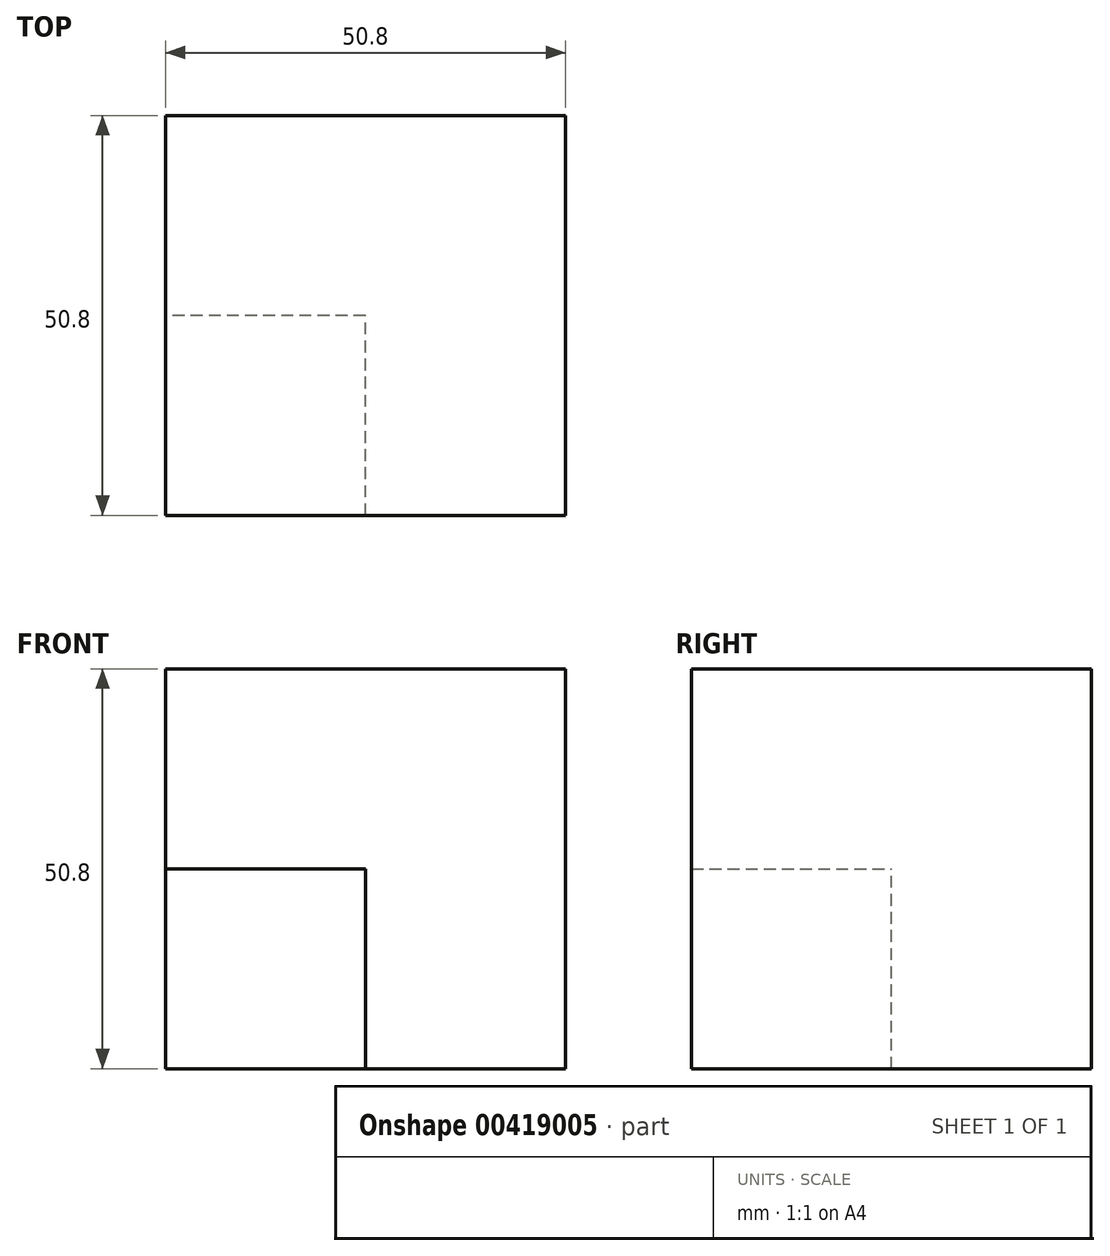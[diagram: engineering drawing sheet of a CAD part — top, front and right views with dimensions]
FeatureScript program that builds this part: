
annotation { "Feature Type Name" : "Feature", "Feature Type Description" : "" }
export const myFeature = defineFeature(function(context is Context, id is Id, definition is map)
    precondition{}
    {
        {
            var Q0;
            Q0=qCreatedBy(makeId("Right.planeOp"),FACE);
            var sketch = newSketch(context, id + "F0", { "sketchPlane" : qUnion([Q0])});
            skLineSegment(sketch, "E0.bottom", {"start": v(0, 0) * mm, "end": v(-25.4, 0) * mm});
            skLineSegment(sketch, "E0.top", {"start": v(0, 50.8) * mm, "end": v(-25.4, 50.8) * mm});
            skLineSegment(sketch, "E0.left", {"start": v(0, 0) * mm, "end": v(0, 50.8) * mm});
            skLineSegment(sketch, "E0.right", {"start": v(-25.4, 0) * mm, "end": v(-25.4, 50.8) * mm});
            skSolve(sketch);
        }
        {
            var Q0;
            Q0=makeQuery(id+"F0.imprint","IMPRINT",FACE,{"disambiguationData":[TD([[makeQuery(id+"F0.imprint","IMPRINT",EDGE,{"derivedFrom":sQuery(id+"F0.wireOp",EDGE,"E0.bottom")}),-1.0]])]});
            extrude(context, id + "F1", {"entities" : qUnion([Q0]), "depth" : 50.8 * mm});
        }
        {
            var Q0;
            Q0=makeQuery(id+"F1.opExtrude","SWEPT_FACE",FACE,{"disambiguationData":[OSD([sQuery(id+"F0.wireOp",EDGE,"E0.right")])]});
            var sketch = newSketch(context, id + "F2", { "sketchPlane" : qUnion([Q0])});
            skLineSegment(sketch, "E1.bottom", {"start": v(0, 0) * mm, "end": v(25.4, 0) * mm});
            skLineSegment(sketch, "E1.top", {"start": v(0, 25.4) * mm, "end": v(25.4, 25.4) * mm});
            skLineSegment(sketch, "E1.left", {"start": v(0, 0) * mm, "end": v(0, 25.4) * mm});
            skLineSegment(sketch, "E1.right", {"start": v(25.4, 0) * mm, "end": v(25.4, 25.4) * mm});
            skSolve(sketch);
        }
        {
            var Q0;
            {var subQ5=sQuery(id+"F2.wireOp",EDGE,"E1.top");Q0=makeQuery(id+"F2.imprint","IMPRINT",FACE,{"disambiguationData":[TD([[makeQuery(id+"F2.imprint","IMPRINT",EDGE,{"derivedFrom":subQ5}),1.0]])]});}
            extrude(context, id + "F3", {"entities" : qUnion([Q0]), "operationType" : NewBodyOperationType.ADD, "depth" : 25.4 * mm});
        }
    });
